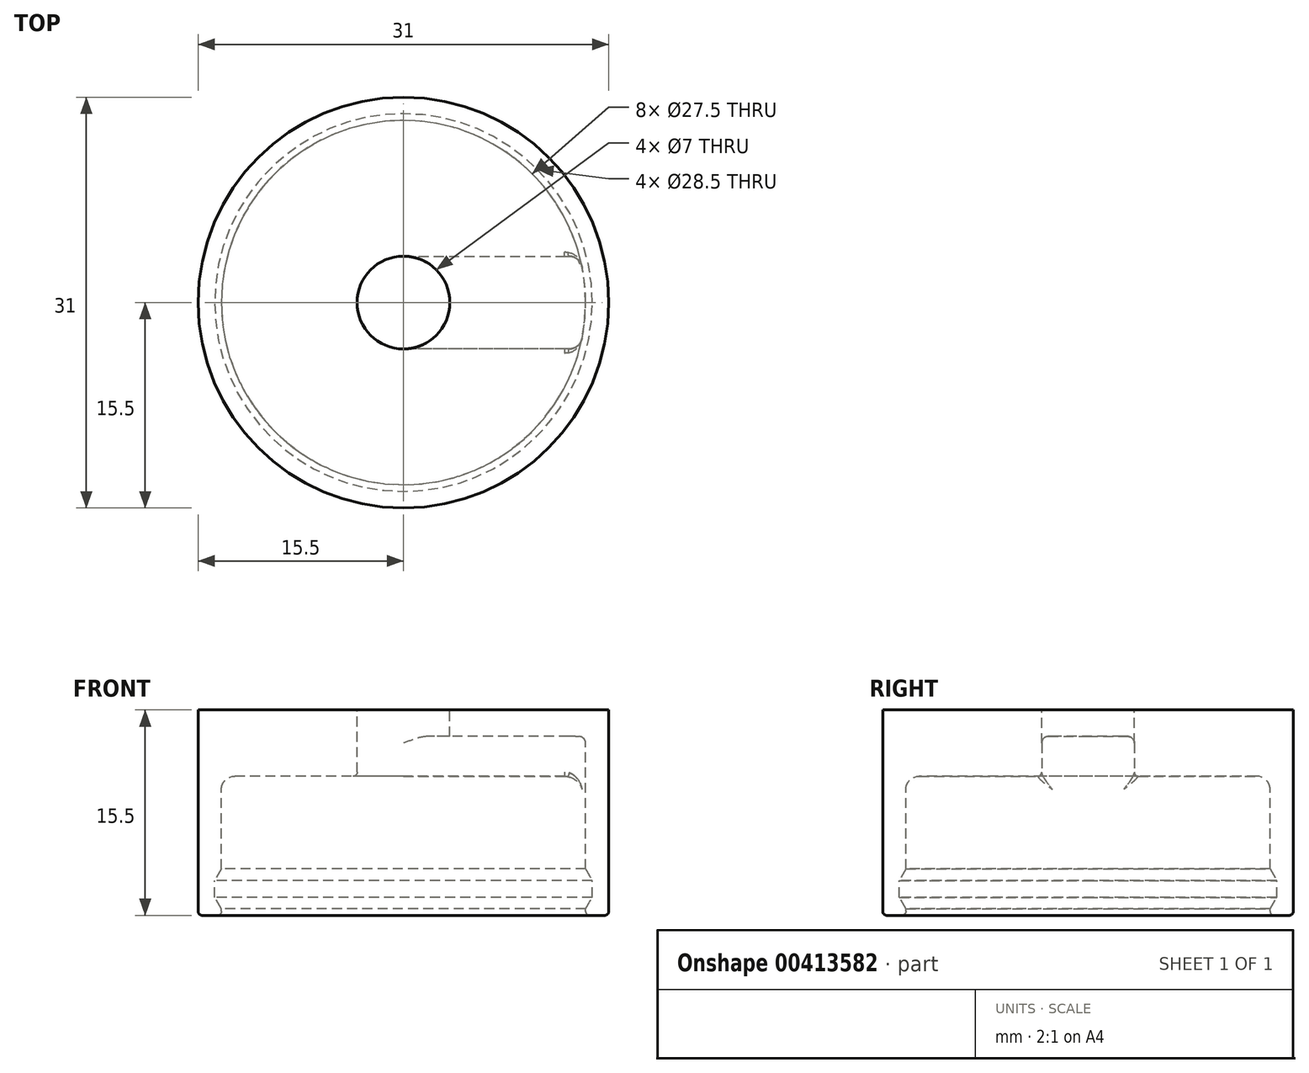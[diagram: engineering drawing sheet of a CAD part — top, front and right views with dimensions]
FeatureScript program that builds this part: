
annotation { "Feature Type Name" : "Feature", "Feature Type Description" : "" }
export const myFeature = defineFeature(function(context is Context, id is Id, definition is map)
    precondition{}
    {
        {
            var Q0;
            Q0=qCreatedBy(makeId("Front.planeOp"),FACE);
            var sketch = newSketch(context, id + "F0", { "sketchPlane" : qUnion([Q0])});
            skLineSegment(sketch, "E0", {"start": v(0, 0) * mm, "end": v(0, -15.5) * mm, "construction": true});
            skLineSegment(sketch, "E1", {"start": v(3.5, 0) * mm, "end": v(3.5, -5) * mm});
            skLineSegment(sketch, "E2", {"start": v(3.5, -5) * mm, "end": v(13.75, -5) * mm});
            skLineSegment(sketch, "E3", {"start": v(13.75, -5) * mm, "end": v(13.75, -12) * mm});
            skLineSegment(sketch, "E4", {"start": v(13.75, -12) * mm, "end": v(14.25, -12.87) * mm});
            skLineSegment(sketch, "E5", {"start": v(14.25, -12.87) * mm, "end": v(14.25, -14.13) * mm});
            skLineSegment(sketch, "E6", {"start": v(14.25, -14.13) * mm, "end": v(13.75, -15) * mm});
            skLineSegment(sketch, "E7", {"start": v(13.75, -15) * mm, "end": v(13.75, -15.5) * mm});
            skLineSegment(sketch, "E8", {"start": v(13.75, -15.5) * mm, "end": v(15.5, -15.5) * mm});
            skLineSegment(sketch, "E9", {"start": v(15.5, -15.5) * mm, "end": v(15.5, 0) * mm});
            skLineSegment(sketch, "E10", {"start": v(15.5, 0) * mm, "end": v(3.5, 0) * mm});
            skSolve(sketch);
        }
        {
            var Q0;
            Q0 = qSketchRegion(id + "F0", true);
            var Q1;
            Q1=sQuery(id+"F0.wireOp",EDGE,"E0");
            revolve(context, id + "F1", {"entities" : qUnion([Q0]), "axis" : qUnion([Q1]), "revolveType" : RevolveType.FULL});
        }
        {
            var Q0;
            Q0=makeQuery(id+"F1.opRevolve","SWEPT_FACE",FACE,{"disambiguationData":[OSD([sQuery(id+"F0.wireOp",EDGE,"E2")])]});
            var sketch = newSketch(context, id + "F2", { "sketchPlane" : qUnion([Q0])});
            skArc(sketch, "E11.0.0", {"start": v(13.3, -3.5) * mm, "mid": v(13.75, 0) * mm, "end": v(13.3, 3.5) * mm});
            skLineSegment(sketch, "E12", {"start": v(13.3, 3.5) * mm, "end": v(0, 3.5) * mm});
            skLineSegment(sketch, "E13", {"start": v(0, 3.5) * mm, "end": v(0, -3.5) * mm});
            skLineSegment(sketch, "E14", {"start": v(0, -3.5) * mm, "end": v(13.3, -3.5) * mm});
            skSolve(sketch);
        }
        {
            var Q0;
            Q0=makeQuery(id+"F2.imprint","IMPRINT",FACE,{"disambiguationData":[TD([[makeQuery(id+"F2.imprint","IMPRINT",EDGE,{"derivedFrom":sQuery(id+"F2.wireOp",EDGE,"E11.0.0")}),-1.0]])]});
            extrude(context, id + "F3", {"entities" : qUnion([Q0]), "operationType" : NewBodyOperationType.REMOVE, "oppositeDirection" : true, "depth" : 3 * mm});
        }
        {
            var Q0;
            Q0=makeQuery(id+"F3.boolean.opBoolean","COPY",EDGE,{"derivedFrom":makeQuery(id+"F3.opExtrude","SWEPT_EDGE",EDGE,{"disambiguationData":[OSD([sQuery(id+"F0.wireOp",EDGE,"E2"),sQuery(id+"F0.wireOp",EDGE,"E3"),sQuery(id+"F2.wireOp",EDGE,"E11.0.0"),sQuery(id+"F2.wireOp",EDGE,"E12")])]})});
            var Q1;
            Q1=makeQuery(id+"F3.boolean.opBoolean","COPY",EDGE,{"derivedFrom":makeQuery(id+"F3.opExtrude","SWEPT_EDGE",EDGE,{"disambiguationData":[OSD([sQuery(id+"F0.wireOp",EDGE,"E2"),sQuery(id+"F0.wireOp",EDGE,"E3"),sQuery(id+"F2.wireOp",EDGE,"E11.0.0"),sQuery(id+"F2.wireOp",EDGE,"E14")])]})});
            fillet(context, id + "F4", {"entities" : qUnion([Q0, Q1]), "radius" : 1 * mm, "tangentPropagation" : true, "allowEdgeOverflow" : false});
        }
        {
            var Q0;
            Q0=makeQuery(id+"F1.opRevolve","SWEPT_EDGE",EDGE,{"disambiguationData":[OSD([sQuery(id+"F0.wireOp",EDGE,"E2"),sQuery(id+"F0.wireOp",EDGE,"E3")])]});
            fillet(context, id + "F5", {"entities" : qUnion([Q0]), "radius" : 1 * mm, "tangentPropagation" : true, "allowEdgeOverflow" : false});
        }
        {
            var Q0;
            {var subQ0=sQuery(id+"F0.wireOp",EDGE,"E3");var subQ1=sQuery(id+"F0.wireOp",EDGE,"E2");Q0=makeQuery(id+"F5.opFillet","BLEND_EDGE",EDGE,{"blendedFrom":[makeQuery(id+"F1.opRevolve","SWEPT_EDGE",EDGE,{"disambiguationData":[OSD([subQ1,subQ0])]}),makeQuery(id+"F4.opFillet","BLEND_FACE",FACE,{"disambiguationData":[OSD([subQ1,subQ0,sQuery(id+"F2.wireOp",EDGE,"E11.0.0"),sQuery(id+"F2.wireOp",EDGE,"E12")])]})],"blendedInto":[makeQuery(id+"F4.opFillet","BLEND_FACE",FACE,{"disambiguationData":[OSD([subQ1,subQ0,sQuery(id+"F2.wireOp",EDGE,"E11.0.0"),sQuery(id+"F2.wireOp",EDGE,"E12")])]})]});}
            var Q1;
            Q1=makeQuery(id+"F3.boolean.opBoolean","COPY",EDGE,{"derivedFrom":makeQuery(id+"F3.opExtrude","CAP_EDGE",EDGE,{"disambiguationData":[OSD([sQuery(id+"F2.wireOp",EDGE,"E12")])],"isStart":true})});
            fillet(context, id + "F6", {"entities" : qUnion([Q0, Q1]), "radius" : .3 * mm, "tangentPropagation" : true, "allowEdgeOverflow" : false});
        }
        {
            var Q0;
            Q0=makeQuery(id+"F3.boolean.opBoolean","COPY",EDGE,{"derivedFrom":makeQuery(id+"F3.opExtrude","CAP_EDGE",EDGE,{"disambiguationData":[OSD([sQuery(id+"F2.wireOp",EDGE,"E14")])],"isStart":false})});
            var Q1;
            Q1=makeQuery(id+"F3.boolean.opBoolean","COPY",EDGE,{"derivedFrom":makeQuery(id+"F3.opExtrude","CAP_EDGE",EDGE,{"disambiguationData":[OSD([sQuery(id+"F0.wireOp",EDGE,"E1"),sQuery(id+"F0.wireOp",EDGE,"E2")])],"isStart":false})});
            fillet(context, id + "F7", {"entities" : qUnion([Q0, Q1]), "radius" : .5 * mm, "tangentPropagation" : true, "allowEdgeOverflow" : false});
        }
        {
            var Q0;
            Q0=makeQuery(id+"F1.opRevolve","SWEPT_EDGE",EDGE,{"disambiguationData":[OSD([sQuery(id+"F0.wireOp",EDGE,"E8"),sQuery(id+"F0.wireOp",EDGE,"E9")])]});
            var Q1;
            Q1=makeQuery(id+"F1.opRevolve","SWEPT_EDGE",EDGE,{"disambiguationData":[OSD([sQuery(id+"F0.wireOp",EDGE,"E7"),sQuery(id+"F0.wireOp",EDGE,"E8")])]});
            fillet(context, id + "F8", {"entities" : qUnion([Q0, Q1]), "radius" : .3 * mm, "tangentPropagation" : true, "allowEdgeOverflow" : false});
        }
    });
